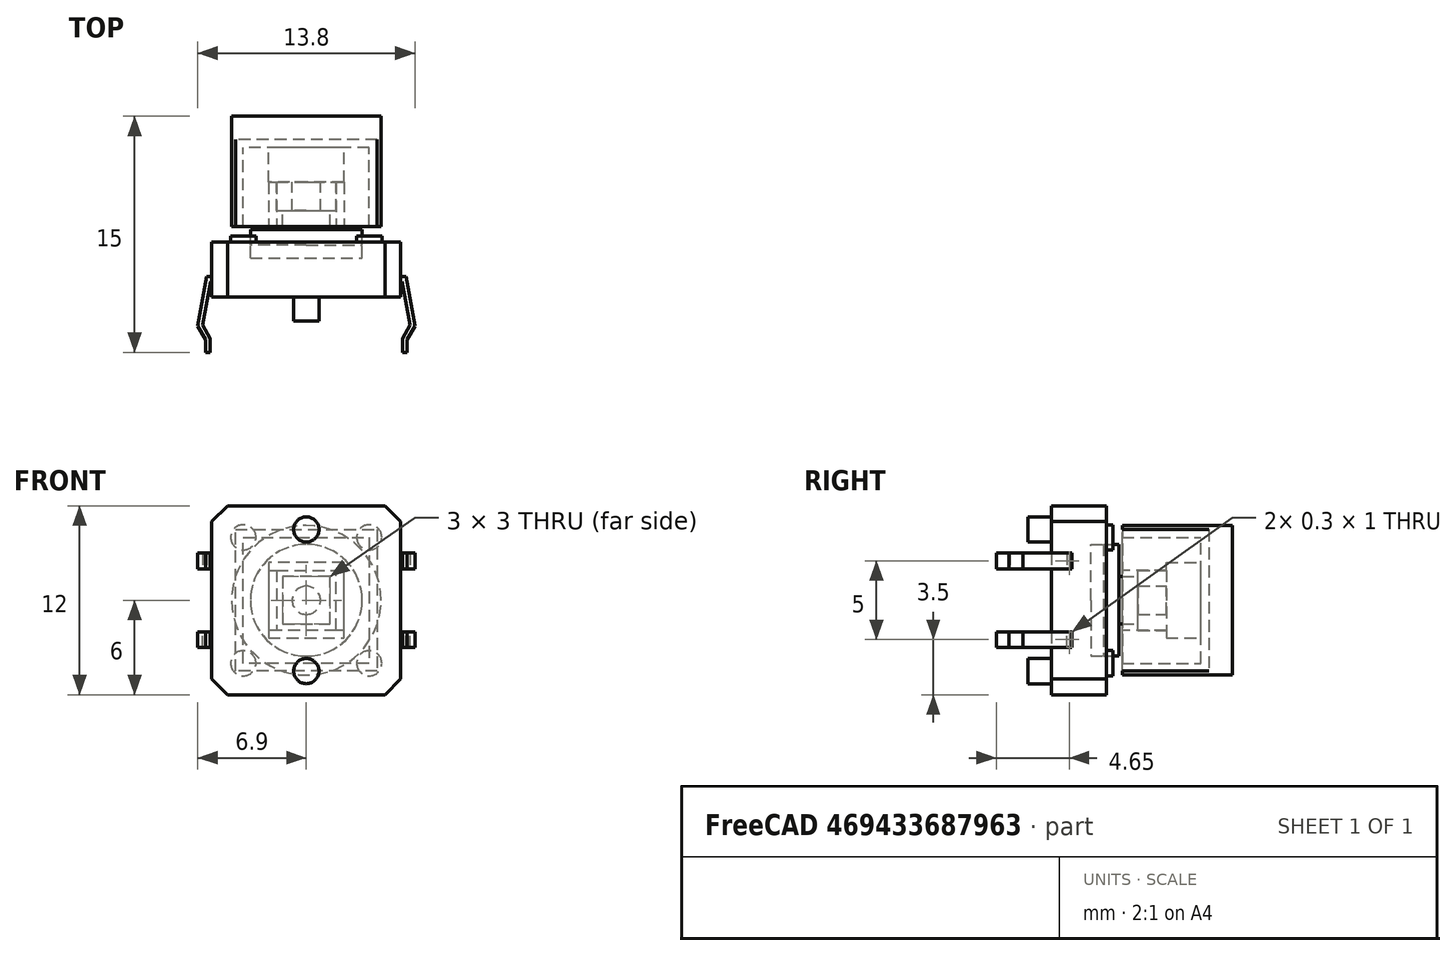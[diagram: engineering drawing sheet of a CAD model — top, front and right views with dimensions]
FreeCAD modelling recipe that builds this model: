
FCSTD DOCUMENT  (FreeCAD 0.18R16131 (Git))
Label: omron-B3F
License: All rights reserved
LicenseURL: http://en.wikipedia.org/wiki/All_rights_reserved
objects: Part::Feature×3, Part::Cylinder×1, Part::Chamfer×1, App::Part×1
note: 5 computed .brp shape members not serialized (recipe doc carries the construction recipe); baked Part::Feature solids carry a one-line shape summary decoded from their .brp

FEATURE [Part::Feature] Part__Feature  label="B3F_4050_BASE"
  shape: bbox 13.8 x 7.4 x 12 mm, 71 faces (baked)
FEATURE [Part::Feature] Part__Feature001  label="B32_1200"
  Placement = pos=(-3.1e-15,10,0) rot=(0,0,1;0rad)
  shape: bbox 9 x 5.5 x 9 mm, 24 faces (baked)
FEATURE [Part::Feature] Part__Feature002  label="B3F_4050_BUTTON"
  Placement = pos=(-3.1e-15,7.3,0) rot=(0,0,1;0rad)
  shape: bbox 7.1 x 4 x 7.1 mm, 17 faces (baked)
FEATURE [Part::Cylinder] Cylinder
  Angle = 360
  AttacherType = Attacher::AttachEngine3D
  Height = 7
  Placement = pos=(0,11.5,0) rot=(1,0,0;1.5708rad)
  Radius = 4.75
FEATURE [Part::Chamfer] Chamfer
  Base = -> Part__Feature
  Edges = 4 edges r=1: [Edge19,Edge21,Edge22,Edge23]
FEATURE [App::Part] B3F_4050
  Group = -> [Part__Feature,Part__Feature001,Part__Feature002,Cylinder,Chamfer]
  Origin = -> Origin
